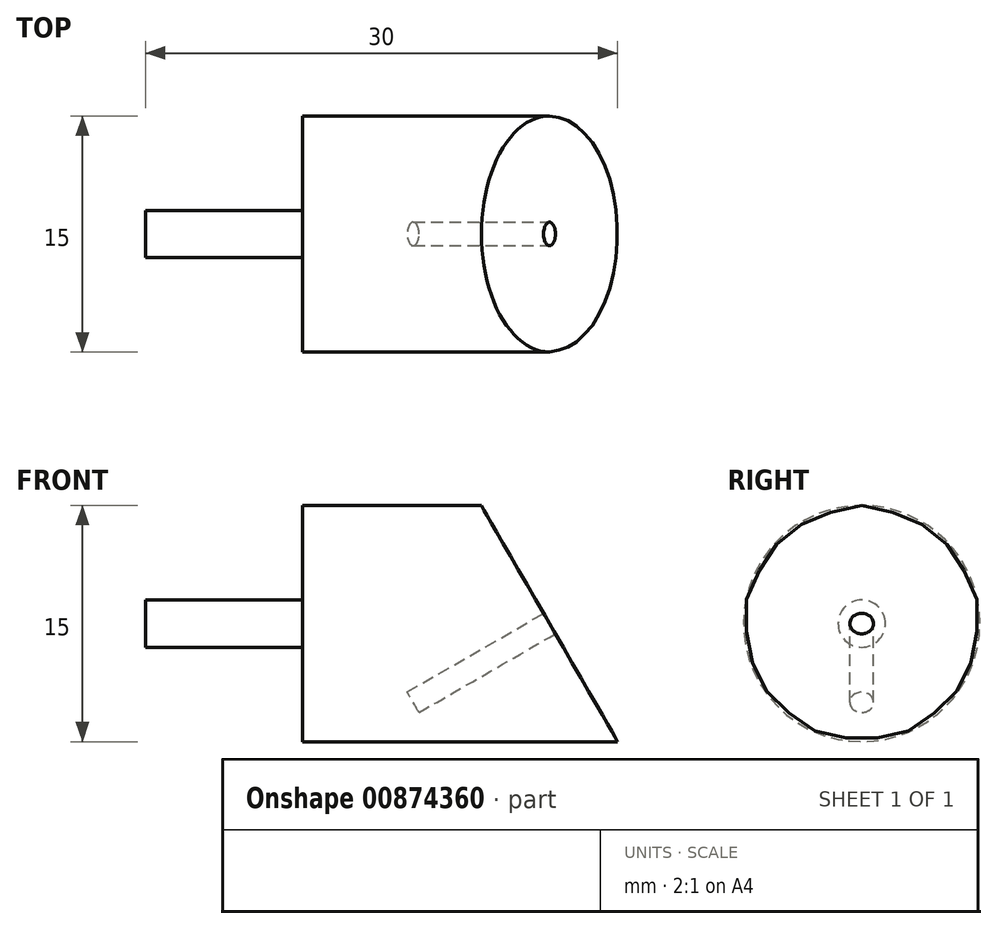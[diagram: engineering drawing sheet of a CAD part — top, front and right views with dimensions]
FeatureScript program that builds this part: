
annotation { "Feature Type Name" : "Feature", "Feature Type Description" : "" }
export const myFeature = defineFeature(function(context is Context, id is Id, definition is map)
    precondition{}
    {
        {
            var Q0;
            Q0=qCreatedBy(makeId("Front.planeOp"),FACE);
            var sketch = newSketch(context, id + "F0", { "sketchPlane" : qUnion([Q0])});
            skLineSegment(sketch, "E0", {"start": v(-40.7, 0) * mm, "end": v(58.25, 0) * mm, "construction": true});
            skLineSegment(sketch, "E1.bottom", {"start": v(10, 7.5) * mm, "end": v(30, 7.5) * mm});
            skLineSegment(sketch, "E1.top", {"start": v(0, 0) * mm, "end": v(30, 0) * mm});
            skLineSegment(sketch, "E1.left", {"start": v(0, 1.5) * mm, "end": v(0, 0) * mm});
            skLineSegment(sketch, "E1.right", {"start": v(30, 7.5) * mm, "end": v(30, 0) * mm});
            skLineSegment(sketch, "E2", {"start": v(10, 7.5) * mm, "end": v(10, 1.5) * mm});
            skLineSegment(sketch, "E3", {"start": v(10, 1.5) * mm, "end": v(0, 1.5) * mm});
            skPoint(sketch, "E4.orphan", {"position": v(0, 7.5) * mm});
            skSolve(sketch);
        }
        {
            var Q0;
            Q0=makeQuery(id+"F0.imprint","IMPRINT",FACE,{"disambiguationData":[TD([[makeQuery(id+"F0.imprint","IMPRINT",EDGE,{"derivedFrom":sQuery(id+"F0.wireOp",EDGE,"E1.bottom")}),-1.0]])]});
            var Q1;
            {var subQ2=sQuery(id+"F0.wireOp",EDGE,"E1.top");Q1=makeQuery(id+"F0.imprint","IMPRINT",FACE,{"disambiguationData":[TD([[makeQuery(id+"F0.imprint","IMPRINT",EDGE,{"derivedFrom":subQ2}),1.0]])]});}
            var Q2;
            Q2=sQuery(id+"F0.wireOp",EDGE,"E0");
            revolve(context, id + "F1", {"surfaceOperationType" : NewSurfaceOperationType.NEW, "entities" : qUnion([Q0, Q1]), "axis" : qUnion([Q2]), "revolveType" : RevolveType.FULL});
        }
        {
            var Q0;
            Q0=qCreatedBy(makeId("Front.planeOp"),FACE);
            var sketch = newSketch(context, id + "F2", { "sketchPlane" : qUnion([Q0])});
            skLineSegment(sketch, "E5", {"start": v(30, -7.5) * mm, "end": v(21.34, 7.5) * mm});
            skLineSegment(sketch, "E6", {"start": v(21.34, 7.5) * mm, "end": v(30, 7.5) * mm});
            skLineSegment(sketch, "E7", {"start": v(30, 7.5) * mm, "end": v(30, -7.5) * mm});
            skSolve(sketch);
        }
        {
            var Q0;
            Q0=qSketchRegion(id+"F2",true);
            extrude(context, id + "F3", {"entities" : qUnion([Q0]), "operationType" : NewBodyOperationType.REMOVE, "endBound" : BoundingType.THROUGH_ALL, "oppositeDirection" : true, "depth" : 25 * mm, "offsetDistance" : 25 * mm, "hasSecondDirection" : true, "secondDirectionBound" : SecondDirectionBoundingType.THROUGH_ALL, "secondDirectionOppositeDirection" : false, "secondDirectionDepth" : 25 * mm});
        }
        {
            var Q0;
            Q0=makeQuery(id+"F3.boolean.opBoolean","COPY",FACE,{"derivedFrom":makeQuery(id+"F3.opExtrude","SWEPT_FACE",FACE,{"disambiguationData":[OSD([sQuery(id+"F2.wireOp",EDGE,"E5")])]})});
            var sketch = newSketch(context, id + "F4", { "sketchPlane" : qUnion([Q0])});
            skCircle(sketch, "E8", {"center": v(0, -12.83) * mm, "radius": 0.75 * mm});
            skSolve(sketch);
        }
        {
            var Q0;
            Q0=makeQuery(id+"F4.imprint","IMPRINT",FACE,{"disambiguationData":[TD([[makeQuery(id+"F4.imprint","IMPRINT",EDGE,{"derivedFrom":sQuery(id+"F4.wireOp",EDGE,"E8")}),1.0]])]});
            extrude(context, id + "F5", {"entities" : qUnion([Q0]), "operationType" : NewBodyOperationType.REMOVE, "oppositeDirection" : true, "depth" : 10 * mm, "offsetDistance" : 25 * mm});
        }
    });
